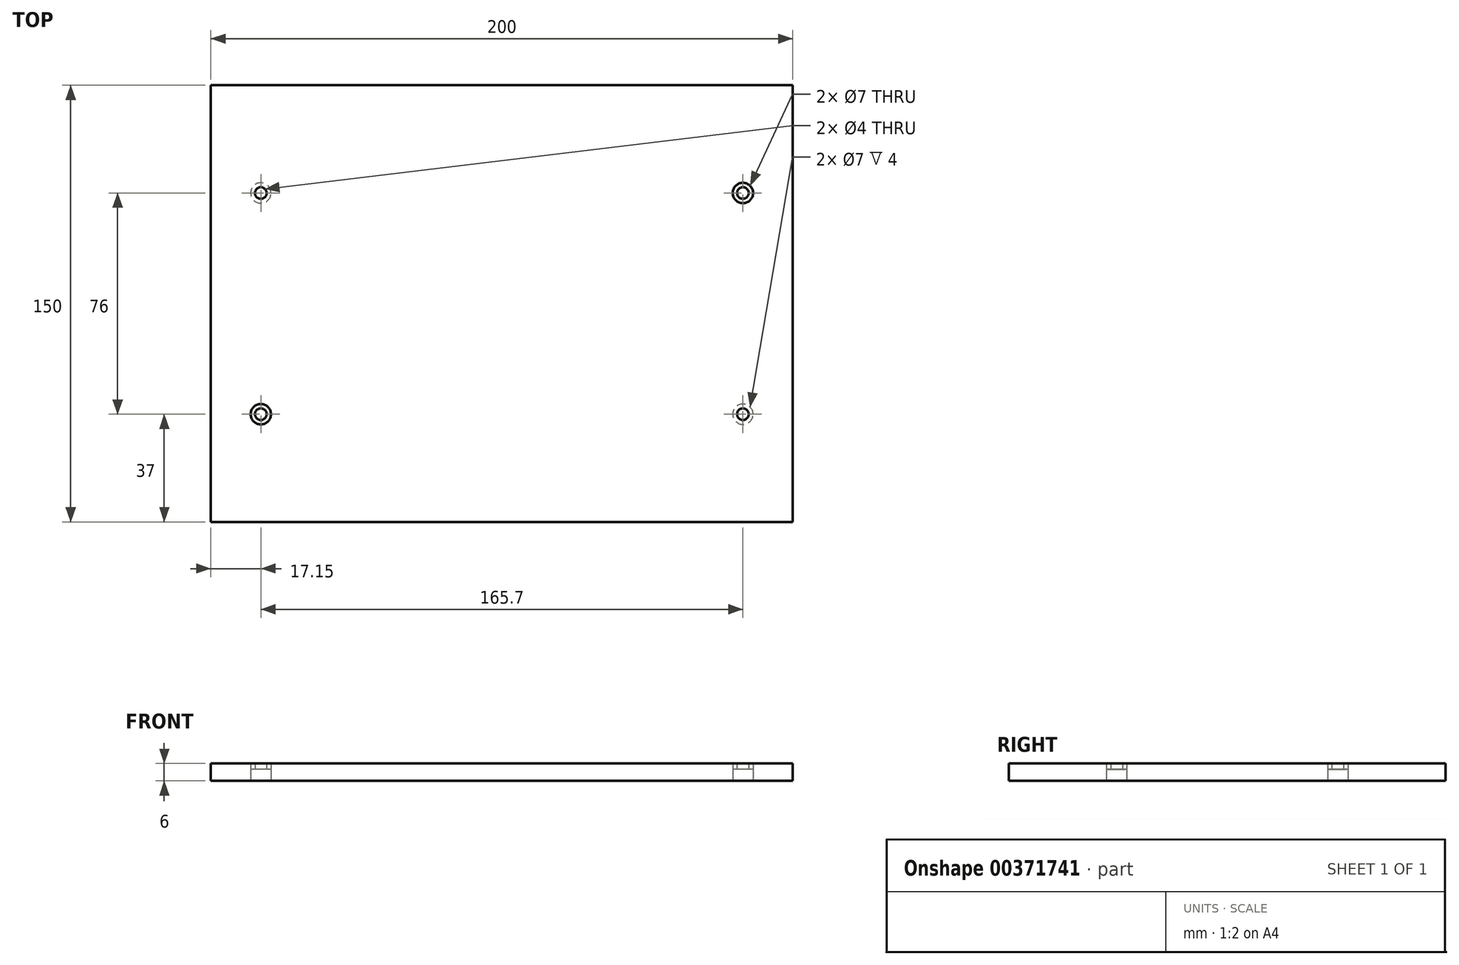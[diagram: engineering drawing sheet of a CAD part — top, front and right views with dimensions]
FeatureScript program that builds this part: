
annotation { "Feature Type Name" : "Feature", "Feature Type Description" : "" }
export const myFeature = defineFeature(function(context is Context, id is Id, definition is map)
    precondition{}
    {
        {
            var Q0;
            Q0=qCreatedBy(makeId("Top.planeOp"),FACE);
            var sketch = newSketch(context, id + "F0", { "sketchPlane" : qUnion([Q0])});
            skLineSegment(sketch, "E0.bottom", {"start": v(-100, 75) * mm, "end": v(100, 75) * mm});
            skLineSegment(sketch, "E0.top", {"start": v(-100, -75) * mm, "end": v(100, -75) * mm});
            skLineSegment(sketch, "E0.left", {"start": v(-100, 75) * mm, "end": v(-100, -75) * mm});
            skLineSegment(sketch, "E0.right", {"start": v(100, 75) * mm, "end": v(100, -75) * mm});
            skPoint(sketch, "E0.middle", {"position": v(0, 0) * mm});
            skLineSegment(sketch, "E1", {"start": v(0, 0) * mm, "end": v(-82.85, 0) * mm, "construction": true});
            skLineSegment(sketch, "E2", {"start": v(-82.85, 0) * mm, "end": v(-82.85, 38) * mm, "construction": true});
            skCircle(sketch, "E3", {"center": v(-82.85, 38) * mm, "radius": 2 * mm});
            skLineSegment(sketch, "E4", {"start": v(0, 0) * mm, "end": v(0, 26.05) * mm, "construction": true});
            skCircle(sketch, "E5.MirrorC", {"center": v(82.85, 38) * mm, "radius": 2 * mm});
            skCircle(sketch, "E6.MirrorC", {"center": v(-82.85, -38) * mm, "radius": 2 * mm});
            skCircle(sketch, "E7.MirrorC", {"center": v(82.85, -38) * mm, "radius": 2 * mm});
            skCircle(sketch, "E8", {"center": v(-82.85, 38) * mm, "radius": 3.5 * mm});
            skCircle(sketch, "E9.MirrorC", {"center": v(82.85, 38) * mm, "radius": 3.5 * mm});
            skCircle(sketch, "E10.MirrorC", {"center": v(-82.85, -38) * mm, "radius": 3.5 * mm});
            skCircle(sketch, "E11.MirrorC", {"center": v(82.85, -38) * mm, "radius": 3.5 * mm});
            skSolve(sketch);
        }
        {
            var Q0;
            Q0=makeQuery(id+"F0.imprint","IMPRINT",FACE,{"disambiguationData":[TD([[makeQuery(id+"F0.imprint","IMPRINT",EDGE,{"derivedFrom":sQuery(id+"F0.wireOp",EDGE,"E0.bottom")}),-1.0]])]});
            var Q1;
            Q1=makeQuery(id+"F0.imprint","IMPRINT",FACE,{"disambiguationData":[TD([[makeQuery(id+"F0.imprint","IMPRINT",EDGE,{"derivedFrom":sQuery(id+"F0.wireOp",EDGE,"E3")}),-1.0]])]});
            var Q2;
            Q2=makeQuery(id+"F0.imprint","IMPRINT",FACE,{"disambiguationData":[TD([[makeQuery(id+"F0.imprint","IMPRINT",EDGE,{"derivedFrom":sQuery(id+"F0.wireOp",EDGE,"E7.MirrorC")}),-1.0]])]});
            var Q3;
            Q3=makeQuery(id+"F0.imprint","IMPRINT",FACE,{"disambiguationData":[TD([[makeQuery(id+"F0.imprint","IMPRINT",EDGE,{"derivedFrom":sQuery(id+"F0.wireOp",EDGE,"E5.MirrorC")}),1.0]])]});
            var Q4;
            Q4=makeQuery(id+"F0.imprint","IMPRINT",FACE,{"disambiguationData":[TD([[makeQuery(id+"F0.imprint","IMPRINT",EDGE,{"derivedFrom":sQuery(id+"F0.wireOp",EDGE,"E6.MirrorC")}),1.0]])]});
            extrude(context, id + "F1", {"entities" : qUnion([Q0, Q1, Q2, Q3, Q4]), "depth" : 6 * mm});
        }
        {
            var Q0;
            Q0=makeQuery(id+"F0.imprint","IMPRINT",FACE,{"disambiguationData":[TD([[makeQuery(id+"F0.imprint","IMPRINT",EDGE,{"derivedFrom":sQuery(id+"F0.wireOp",EDGE,"E3")}),-1.0]])]});
            var Q1;
            Q1=makeQuery(id+"F0.imprint","IMPRINT",FACE,{"disambiguationData":[TD([[makeQuery(id+"F0.imprint","IMPRINT",EDGE,{"derivedFrom":sQuery(id+"F0.wireOp",EDGE,"E5.MirrorC")}),1.0]])]});
            var Q2;
            Q2=makeQuery(id+"F0.imprint","IMPRINT",FACE,{"disambiguationData":[TD([[makeQuery(id+"F0.imprint","IMPRINT",EDGE,{"derivedFrom":sQuery(id+"F0.wireOp",EDGE,"E7.MirrorC")}),-1.0]])]});
            var Q3;
            Q3=makeQuery(id+"F0.imprint","IMPRINT",FACE,{"disambiguationData":[TD([[makeQuery(id+"F0.imprint","IMPRINT",EDGE,{"derivedFrom":sQuery(id+"F0.wireOp",EDGE,"E6.MirrorC")}),1.0]])]});
            extrude(context, id + "F2", {"entities" : qUnion([Q0, Q1, Q2, Q3]), "operationType" : NewBodyOperationType.REMOVE, "depth" : 4 * mm});
        }
    });
